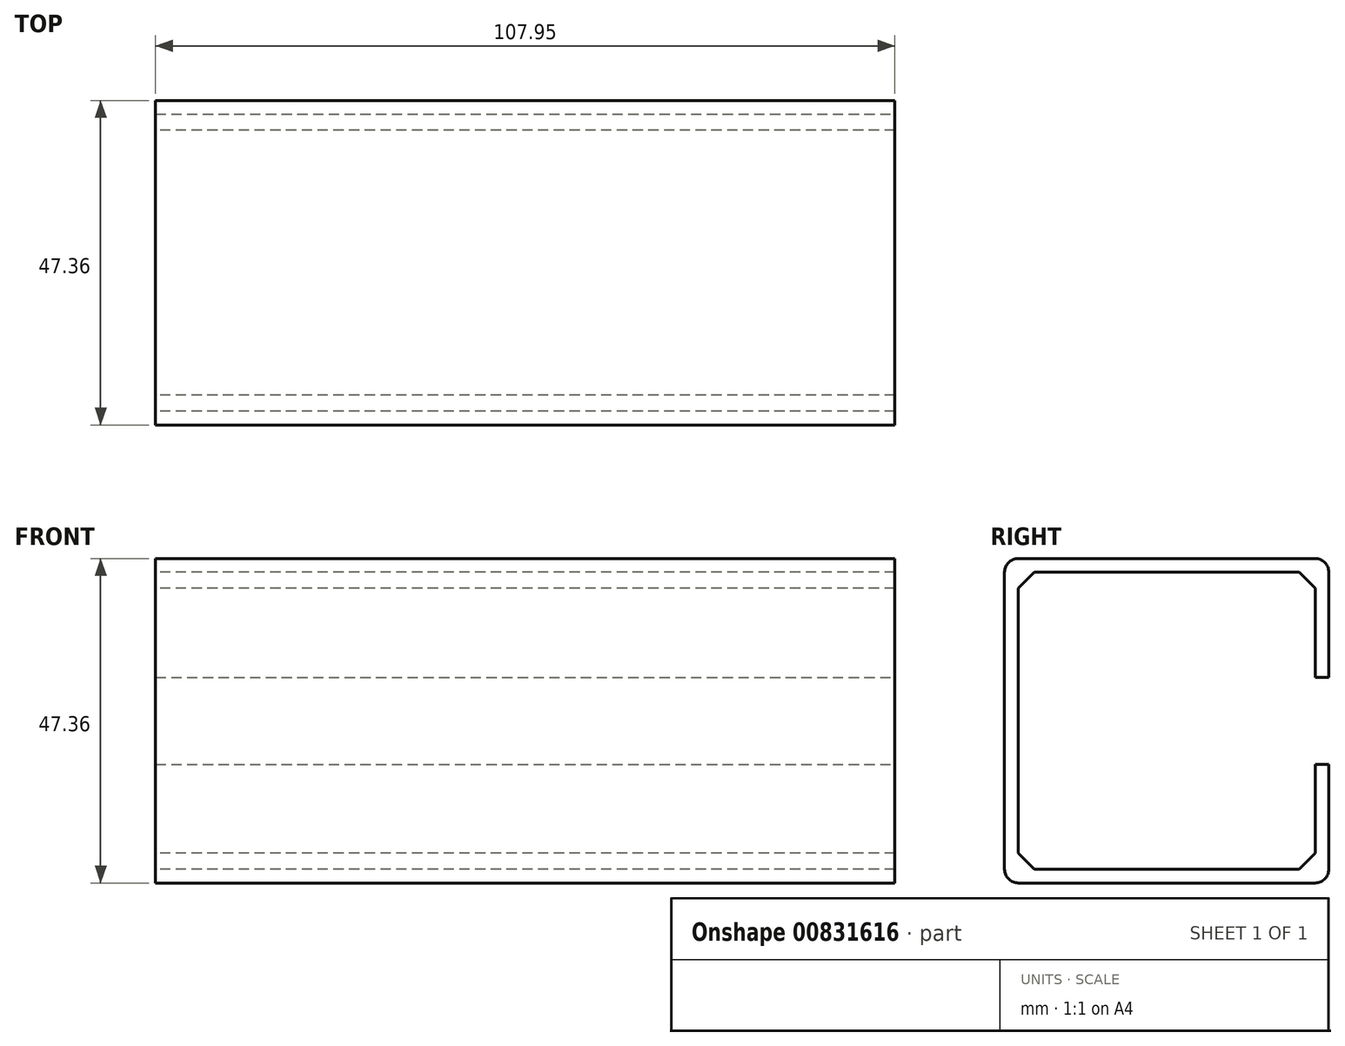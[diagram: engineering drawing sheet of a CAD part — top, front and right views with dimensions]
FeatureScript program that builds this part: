
annotation { "Feature Type Name" : "Feature", "Feature Type Description" : "" }
export const myFeature = defineFeature(function(context is Context, id is Id, definition is map)
    precondition{}
    {
        {
            assignVariable(context, id + "F0", {"name" : "WallWidth", "anyValue" : 2 * mm});
        }
        {
            var Q0;
            Q0=qCreatedBy(makeId("Right.planeOp"),FACE);
            var sketch = newSketch(context, id + "F1", { "sketchPlane" : qUnion([Q0])});
            skLineSegment(sketch, "E0.bottom", {"start": v(21.68, 21.68) * mm, "end": v(-21.68, 21.68) * mm});
            skLineSegment(sketch, "E0.top", {"start": v(21.68, -21.68) * mm, "end": v(-21.68, -21.68) * mm});
            skLineSegment(sketch, "E0.left", {"start": v(21.68, 21.68) * mm, "end": v(21.68, -21.68) * mm});
            skLineSegment(sketch, "E0.right", {"start": v(-21.68, 21.68) * mm, "end": v(-21.68, -21.68) * mm});
            skPoint(sketch, "E0.middle", {"position": v(0, 0) * mm});
            skLineSegment(sketch, "E1", {"start": v(-21.68, -19.34) * mm, "end": v(-19.34, -21.68) * mm});
            skLineSegment(sketch, "E2", {"start": v(19.34, -21.67) * mm, "end": v(21.67, -19.34) * mm});
            skLineSegment(sketch, "E3", {"start": v(-21.67, 19.34) * mm, "end": v(-19.34, 21.68) * mm});
            skLineSegment(sketch, "E4", {"start": v(19.34, 21.68) * mm, "end": v(21.67, 19.34) * mm});
            skLineSegment(sketch, "E5.bottom", {"start": v(-23.68, 23.68) * mm, "end": v(23.68, 23.68) * mm});
            skLineSegment(sketch, "E5.top", {"start": v(-23.68, -23.68) * mm, "end": v(23.68, -23.68) * mm});
            skLineSegment(sketch, "E5.left", {"start": v(-23.68, 23.68) * mm, "end": v(-23.68, -23.67) * mm});
            skLineSegment(sketch, "E5.right", {"start": v(23.68, 23.68) * mm, "end": v(23.68, -23.67) * mm});
            skSolve(sketch);
        }
        {
            var Q0;
            Q0=makeQuery(id+"F1.imprint","IMPRINT",FACE,{"disambiguationData":[TD([[makeQuery(id+"F1.imprint","IMPRINT",EDGE,{"derivedFrom":sQuery(id+"F1.wireOp",EDGE,"E5.bottom")}),-1.0]])]});
            var Q1;
            {var subQ0=sQuery(id+"F1.wireOp",EDGE,"E1");Q1=makeQuery(id+"F1.imprint","IMPRINT",FACE,{"disambiguationData":[TD([[makeQuery(id+"F1.imprint","IMPRINT",EDGE,{"derivedFrom":subQ0}),1.0]])]});}
            var Q2;
            {var subQ3=sQuery(id+"F1.wireOp",EDGE,"E1");Q2=makeQuery(id+"F1.imprint","IMPRINT",FACE,{"disambiguationData":[TD([[makeQuery(id+"F1.imprint","IMPRINT",EDGE,{"derivedFrom":subQ3}),-1.0]])]});}
            var Q3;
            {var subQ3=sQuery(id+"F1.wireOp",EDGE,"E2");Q3=makeQuery(id+"F1.imprint","IMPRINT",FACE,{"disambiguationData":[TD([[makeQuery(id+"F1.imprint","IMPRINT",EDGE,{"derivedFrom":subQ3}),-1.0]])]});}
            var Q4;
            {var subQ3=sQuery(id+"F1.wireOp",EDGE,"E4");Q4=makeQuery(id+"F1.imprint","IMPRINT",FACE,{"disambiguationData":[TD([[makeQuery(id+"F1.imprint","IMPRINT",EDGE,{"derivedFrom":subQ3}),1.0]])]});}
            var Q5;
            {var subQ3=sQuery(id+"F1.wireOp",EDGE,"E3");Q5=makeQuery(id+"F1.imprint","IMPRINT",FACE,{"disambiguationData":[TD([[makeQuery(id+"F1.imprint","IMPRINT",EDGE,{"derivedFrom":subQ3}),1.0]])]});}
            extrude(context, id + "F2", {"entities" : qUnion([Q0, Q1, Q2, Q3, Q4, Q5]), "depth" : getVariable(context, 'WallWidth')});
        }
        {
            var Q0;
            Q0=makeQuery(id+"F1.imprint","IMPRINT",FACE,{"disambiguationData":[TD([[makeQuery(id+"F1.imprint","IMPRINT",EDGE,{"derivedFrom":sQuery(id+"F1.wireOp",EDGE,"E5.bottom")}),-1.0]])]});
            var Q1;
            {var subQ3=sQuery(id+"F1.wireOp",EDGE,"E4");Q1=makeQuery(id+"F1.imprint","IMPRINT",FACE,{"disambiguationData":[TD([[makeQuery(id+"F1.imprint","IMPRINT",EDGE,{"derivedFrom":subQ3}),1.0]])]});}
            var Q2;
            {var subQ3=sQuery(id+"F1.wireOp",EDGE,"E2");Q2=makeQuery(id+"F1.imprint","IMPRINT",FACE,{"disambiguationData":[TD([[makeQuery(id+"F1.imprint","IMPRINT",EDGE,{"derivedFrom":subQ3}),-1.0]])]});}
            var Q3;
            {var subQ3=sQuery(id+"F1.wireOp",EDGE,"E1");Q3=makeQuery(id+"F1.imprint","IMPRINT",FACE,{"disambiguationData":[TD([[makeQuery(id+"F1.imprint","IMPRINT",EDGE,{"derivedFrom":subQ3}),-1.0]])]});}
            var Q4;
            {var subQ3=sQuery(id+"F1.wireOp",EDGE,"E3");Q4=makeQuery(id+"F1.imprint","IMPRINT",FACE,{"disambiguationData":[TD([[makeQuery(id+"F1.imprint","IMPRINT",EDGE,{"derivedFrom":subQ3}),1.0]])]});}
            var Q5;
            Q5 = qSketchRegion(id + "F4", true);
            extrude(context, id + "F3", {"entities" : qUnion([Q0, Q1, Q2, Q3, Q4, Q5]), "operationType" : NewBodyOperationType.ADD, "offsetDistance" : 25 * mm, "depth" : 107.95 * mm});
        }
        {
            var Q0;
            Q0=qSketchRegion(id+"F1",true);
            var sketch = newSketch(context, id + "F4", { "sketchPlane" : qUnion([Q0])});
            skCircle(sketch, "E6", {"center": v(0, 0) * mm, "radius": 6.35 * mm});
            skSolve(sketch);
        }
        {
            var Q0;
            Q0=qSketchRegion(id+"F4",true);
            var sketch = newSketch(context, id + "F5", { "sketchPlane" : qUnion([Q0])});
            skSolve(sketch);
        }
        {
            var Q0;
            {var subQ0=sQuery(id+"F1.wireOp",EDGE,"E1");Q0=makeQuery(id+"F1.imprint","IMPRINT",FACE,{"disambiguationData":[TD([[makeQuery(id+"F1.imprint","IMPRINT",EDGE,{"derivedFrom":subQ0}),1.0]])]});}
            var sketch = newSketch(context, id + "F6", { "sketchPlane" : qUnion([Q0])});
            skSolve(sketch);
        }
        {
            var Q0;
            Q0=qSketchRegion(id+"F5",true);
            var Q1;
            Q1=makeQuery(id+"F4.imprint","IMPRINT",FACE,{"disambiguationData":[TD([[makeQuery(id+"F4.imprint","IMPRINT",EDGE,{"derivedFrom":sQuery(id+"F4.wireOp",EDGE,"E6")}),1.0]])]});
            extrude(context, id + "F7", {"entities" : qUnion([Q0, Q1]), "operationType" : NewBodyOperationType.REMOVE, "endBound" : BoundingType.THROUGH_ALL, "depth" : 25 * mm});
        }
        {
            var Q0;
            {var subQ0=sQuery(id+"F1.wireOp",EDGE,"E5.right");Q0=makeQuery(id+"F3.boolean.opBoolean","MERGE",FACE,{"derivedFrom":[makeQuery(id+"F2.opExtrude","SWEPT_FACE",FACE,{"disambiguationData":[OSD([subQ0])]}),makeQuery(id+"F3.opExtrude","SWEPT_FACE",FACE,{"disambiguationData":[OSD([subQ0])]})]});}
            var sketch = newSketch(context, id + "F8", { "sketchPlane" : qUnion([Q0])});
            skCircle(sketch, "E7", {"center": v(-94.95, 0) * mm, "radius": 6.35 * mm});
            skSolve(sketch);
        }
        {
            var Q0;
            Q0=makeQuery(id+"F8.imprint","IMPRINT",FACE,{"disambiguationData":[TD([[makeQuery(id+"F8.imprint","IMPRINT",EDGE,{"derivedFrom":sQuery(id+"F8.wireOp",EDGE,"E7")}),1.0]])]});
            extrude(context, id + "F9", {"entities" : qUnion([Q0]), "operationType" : NewBodyOperationType.REMOVE, "oppositeDirection" : true, "depth" : 25 * mm});
        }
        {
            var Q0;
            {var subQ0=sQuery(id+"F1.wireOp",EDGE,"E5.left");var subQ1=sQuery(id+"F1.wireOp",EDGE,"E5.bottom");Q0=makeQuery(id+"F3.boolean.opBoolean","MERGE",EDGE,{"derivedFrom":[makeQuery(id+"F2.opExtrude","SWEPT_EDGE",EDGE,{"disambiguationData":[OSD([subQ1,subQ0])]}),makeQuery(id+"F3.opExtrude","SWEPT_EDGE",EDGE,{"disambiguationData":[OSD([subQ1,subQ0])]})]});}
            var Q1;
            {var subQ0=sQuery(id+"F1.wireOp",EDGE,"E5.right");var subQ1=sQuery(id+"F1.wireOp",EDGE,"E5.bottom");Q1=makeQuery(id+"F3.boolean.opBoolean","MERGE",EDGE,{"derivedFrom":[makeQuery(id+"F2.opExtrude","SWEPT_EDGE",EDGE,{"disambiguationData":[OSD([subQ1,subQ0])]}),makeQuery(id+"F3.opExtrude","SWEPT_EDGE",EDGE,{"disambiguationData":[OSD([subQ1,subQ0])]})]});}
            var Q2;
            {var subQ0=sQuery(id+"F1.wireOp",EDGE,"E5.right");var subQ1=sQuery(id+"F1.wireOp",EDGE,"E5.top");Q2=makeQuery(id+"F3.boolean.opBoolean","MERGE",EDGE,{"derivedFrom":[makeQuery(id+"F2.opExtrude","SWEPT_EDGE",EDGE,{"disambiguationData":[OSD([subQ1,subQ0])]}),makeQuery(id+"F3.opExtrude","SWEPT_EDGE",EDGE,{"disambiguationData":[OSD([subQ1,subQ0])]})]});}
            var Q3;
            {var subQ0=sQuery(id+"F1.wireOp",EDGE,"E5.left");var subQ1=sQuery(id+"F1.wireOp",EDGE,"E5.top");Q3=makeQuery(id+"F3.boolean.opBoolean","MERGE",EDGE,{"derivedFrom":[makeQuery(id+"F2.opExtrude","SWEPT_EDGE",EDGE,{"disambiguationData":[OSD([subQ1,subQ0])]}),makeQuery(id+"F3.opExtrude","SWEPT_EDGE",EDGE,{"disambiguationData":[OSD([subQ1,subQ0])]})]});}
            fillet(context, id + "F10", {"entities" : qUnion([Q0, Q1, Q2, Q3]), "radius" : 2 * mm, "tangentPropagation" : true, "allowEdgeOverflow" : false});
        }
        {
            var Q0;
            Q0=makeQuery(id+"F3.opExtrude","CAP_FACE",FACE,{"disambiguationData":[OSD([sQuery(id+"F1.wireOp",EDGE,"E0.bottom"),sQuery(id+"F1.wireOp",EDGE,"E0.top"),sQuery(id+"F1.wireOp",EDGE,"E0.left"),sQuery(id+"F1.wireOp",EDGE,"E0.right"),sQuery(id+"F1.wireOp",EDGE,"E1"),sQuery(id+"F1.wireOp",EDGE,"E2"),sQuery(id+"F1.wireOp",EDGE,"E3"),sQuery(id+"F1.wireOp",EDGE,"E4"),sQuery(id+"F1.wireOp",EDGE,"E5.bottom"),sQuery(id+"F1.wireOp",EDGE,"E5.top"),sQuery(id+"F1.wireOp",EDGE,"E5.left"),sQuery(id+"F1.wireOp",EDGE,"E5.right")])],"isStart":false});
            var sketch = newSketch(context, id + "F11", { "sketchPlane" : qUnion([Q0])});
            skLineSegment(sketch, "E8.bottom", {"start": v(23.68, -6.35) * mm, "end": v(21.68, -6.35) * mm});
            skLineSegment(sketch, "E8.top", {"start": v(23.68, 6.35) * mm, "end": v(21.68, 6.35) * mm});
            skLineSegment(sketch, "E8.left", {"start": v(23.68, -6.35) * mm, "end": v(23.68, 6.35) * mm});
            skLineSegment(sketch, "E8.right", {"start": v(21.68, -6.35) * mm, "end": v(21.68, 6.35) * mm});
            skPoint(sketch, "E9", {"position": v(21.68, 0) * mm});
            skSolve(sketch);
        }
        {
            var Q0;
            Q0=makeQuery(id+"F11.imprint","IMPRINT",FACE,{"disambiguationData":[TD([[makeQuery(id+"F11.imprint","IMPRINT",EDGE,{"derivedFrom":sQuery(id+"F11.wireOp",EDGE,"E8.bottom")}),-1.0]])]});
            extrude(context, id + "F12", {"entities" : qUnion([Q0]), "operationType" : NewBodyOperationType.REMOVE, "endBound" : BoundingType.THROUGH_ALL, "oppositeDirection" : true, "offsetDistance" : 25 * mm, "depth" : 101.6 * mm});
        }
        {
            var Q0;
            {var subQ0=sQuery(id+"F1.wireOp",EDGE,"E1");Q0=makeQuery(id+"F1.imprint","IMPRINT",FACE,{"disambiguationData":[TD([[makeQuery(id+"F1.imprint","IMPRINT",EDGE,{"derivedFrom":subQ0}),1.0]])]});}
            extrude(context, id + "F13", {"entities" : qUnion([Q0]), "operationType" : NewBodyOperationType.REMOVE, "depth" : 25 * mm, "offsetDistance" : 25 * mm});
        }
    });
